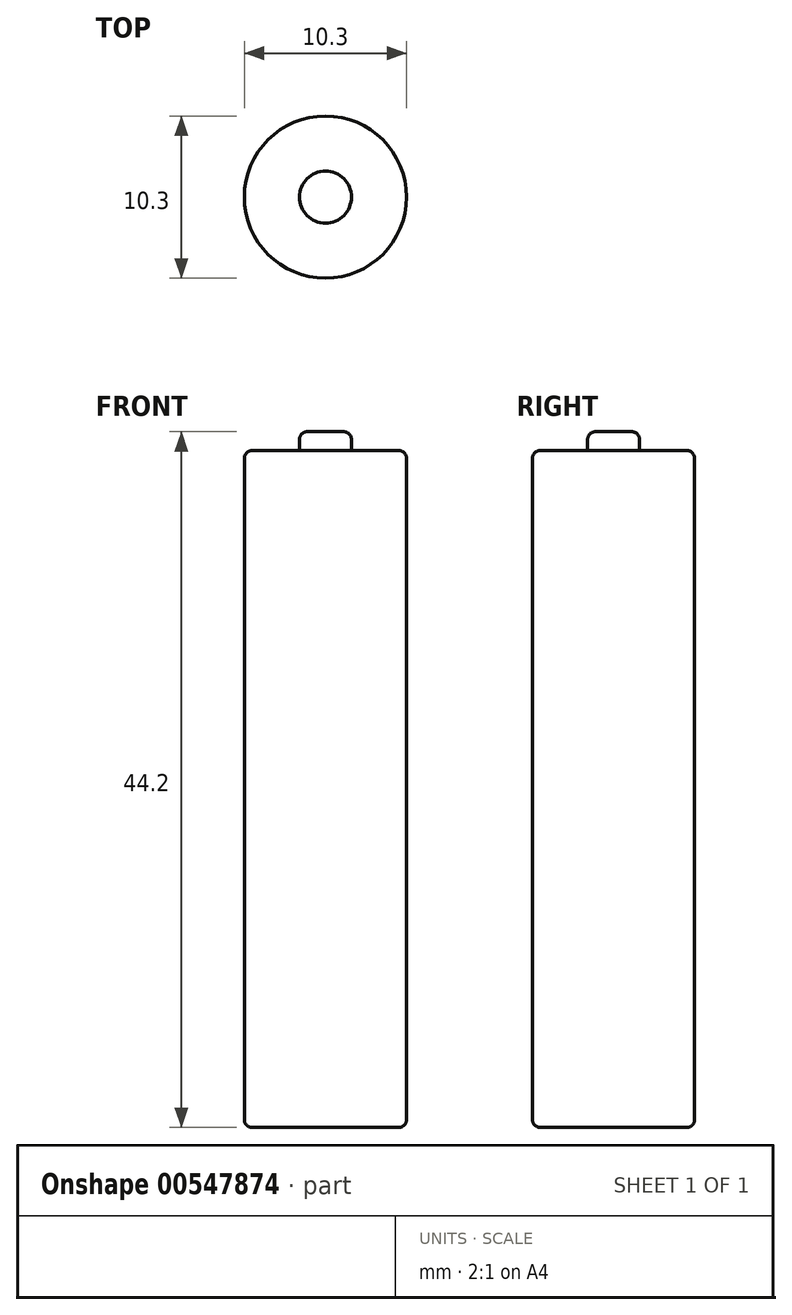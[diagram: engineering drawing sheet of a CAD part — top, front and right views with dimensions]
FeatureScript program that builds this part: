
annotation { "Feature Type Name" : "Feature", "Feature Type Description" : "" }
export const myFeature = defineFeature(function(context is Context, id is Id, definition is map)
    precondition{}
    {
        {
            var Q0;
            Q0=qCreatedBy(makeId("Front.planeOp"),FACE);
            var sketch = newSketch(context, id + "F0", { "sketchPlane" : qUnion([Q0])});
            skLineSegment(sketch, "E0", {"start": v(0, 0) * mm, "end": v(-5.15, 0) * mm});
            skLineSegment(sketch, "E1", {"start": v(-5.15, 0) * mm, "end": v(-5.15, 43) * mm});
            skLineSegment(sketch, "E2", {"start": v(-5.15, 43) * mm, "end": v(-1.65, 43) * mm});
            skLineSegment(sketch, "E3", {"start": v(-1.65, 43) * mm, "end": v(-1.65, 44.2) * mm});
            skLineSegment(sketch, "E4", {"start": v(-1.65, 44.2) * mm, "end": v(0, 44.2) * mm});
            skLineSegment(sketch, "E5", {"start": v(0, 44.2) * mm, "end": v(0, 0) * mm});
            skSolve(sketch);
        }
        {
            var Q0;
            Q0=makeQuery(id+"F0.imprint","IMPRINT",FACE,{"disambiguationData":[TD([[makeQuery(id+"F0.imprint","IMPRINT",EDGE,{"derivedFrom":sQuery(id+"F0.wireOp",EDGE,"E0")}),-1.0]])]});
            var Q1;
            Q1=sQuery(id+"F0.wireOp",EDGE,"E5");
            revolve(context, id + "F1", {"surfaceOperationType" : NewSurfaceOperationType.NEW, "entities" : qUnion([Q0]), "axis" : qUnion([Q1]), "revolveType" : RevolveType.FULL});
        }
        {
            var Q0;
            Q0=makeQuery(id+"F1.opRevolve","SWEPT_EDGE",EDGE,{"disambiguationData":[OSD([sQuery(id+"F0.wireOp",EDGE,"E1"),sQuery(id+"F0.wireOp",EDGE,"E2")])]});
            var Q1;
            Q1=makeQuery(id+"F1.opRevolve","SWEPT_EDGE",EDGE,{"disambiguationData":[OSD([sQuery(id+"F0.wireOp",EDGE,"E0"),sQuery(id+"F0.wireOp",EDGE,"E1")])]});
            var Q2;
            Q2=makeQuery(id+"F1.opRevolve","SWEPT_EDGE",EDGE,{"disambiguationData":[OSD([sQuery(id+"F0.wireOp",EDGE,"E3"),sQuery(id+"F0.wireOp",EDGE,"E4")])]});
            fillet(context, id + "F2", {"entities" : qUnion([Q0, Q1, Q2]), "radius" : 0.5 * mm, "tangentPropagation" : true, "allowEdgeOverflow" : false});
        }
    });
